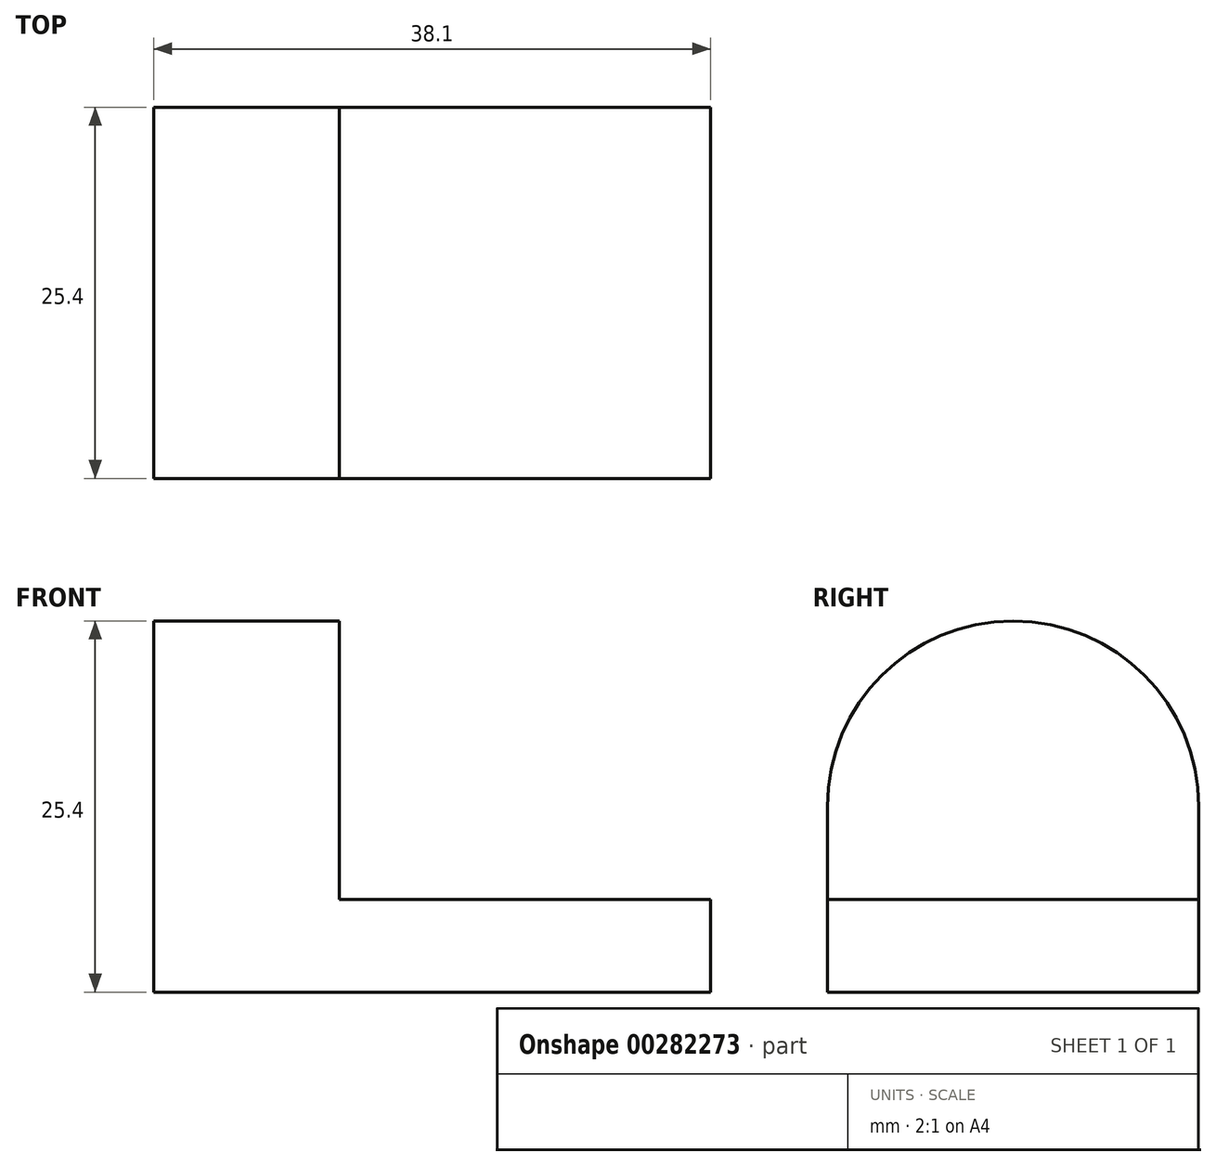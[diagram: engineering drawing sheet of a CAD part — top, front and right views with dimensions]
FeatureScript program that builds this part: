
annotation { "Feature Type Name" : "Feature", "Feature Type Description" : "" }
export const myFeature = defineFeature(function(context is Context, id is Id, definition is map)
    precondition{}
    {
        {
            var Q0;
            Q0=qCreatedBy(makeId("Top.planeOp"),FACE);
            var sketch = newSketch(context, id + "F0", { "sketchPlane" : qUnion([Q0])});
            skLineSegment(sketch, "E0.bottom", {"start": v(0, 0) * mm, "end": v(38.1, 0) * mm});
            skLineSegment(sketch, "E0.top", {"start": v(0, 25.4) * mm, "end": v(38.1, 25.4) * mm});
            skLineSegment(sketch, "E0.left", {"start": v(0, 0) * mm, "end": v(0, 25.4) * mm});
            skLineSegment(sketch, "E0.right", {"start": v(38.1, 0) * mm, "end": v(38.1, 25.4) * mm});
            skSolve(sketch);
        }
        {
            var Q0;
            Q0 = qSketchRegion(id + "F0", true);
            extrude(context, id + "F1", {"entities" : qUnion([Q0]), "depth" : 6.35 * mm});
        }
        {
            var Q0;
            Q0=makeQuery(id+"F1.opExtrude","SWEPT_FACE",FACE,{"disambiguationData":[OSD([sQuery(id+"F0.wireOp",EDGE,"E0.left")])]});
            var sketch = newSketch(context, id + "F2", { "sketchPlane" : qUnion([Q0])});
            skLineSegment(sketch, "E1", {"start": v(-25.4, 6.35) * mm, "end": v(-25.4, 12.7) * mm});
            skArc(sketch, "E2", {"start": v(0, 12.7) * mm, "mid": v(-12.7, 25.4) * mm, "end": v(-25.4, 12.7) * mm});
            skLineSegment(sketch, "E3", {"start": v(0, 12.7) * mm, "end": v(0, 6.35) * mm});
            skLineSegment(sketch, "E4", {"start": v(0, 6.35) * mm, "end": v(-25.4, 6.35) * mm});
            skSolve(sketch);
        }
        {
            var Q0;
            Q0 = qSketchRegion(id + "F2", true);
            extrude(context, id + "F3", {"entities" : qUnion([Q0]), "operationType" : NewBodyOperationType.ADD, "oppositeDirection" : true, "depth" : 12.7 * mm});
        }
    });
